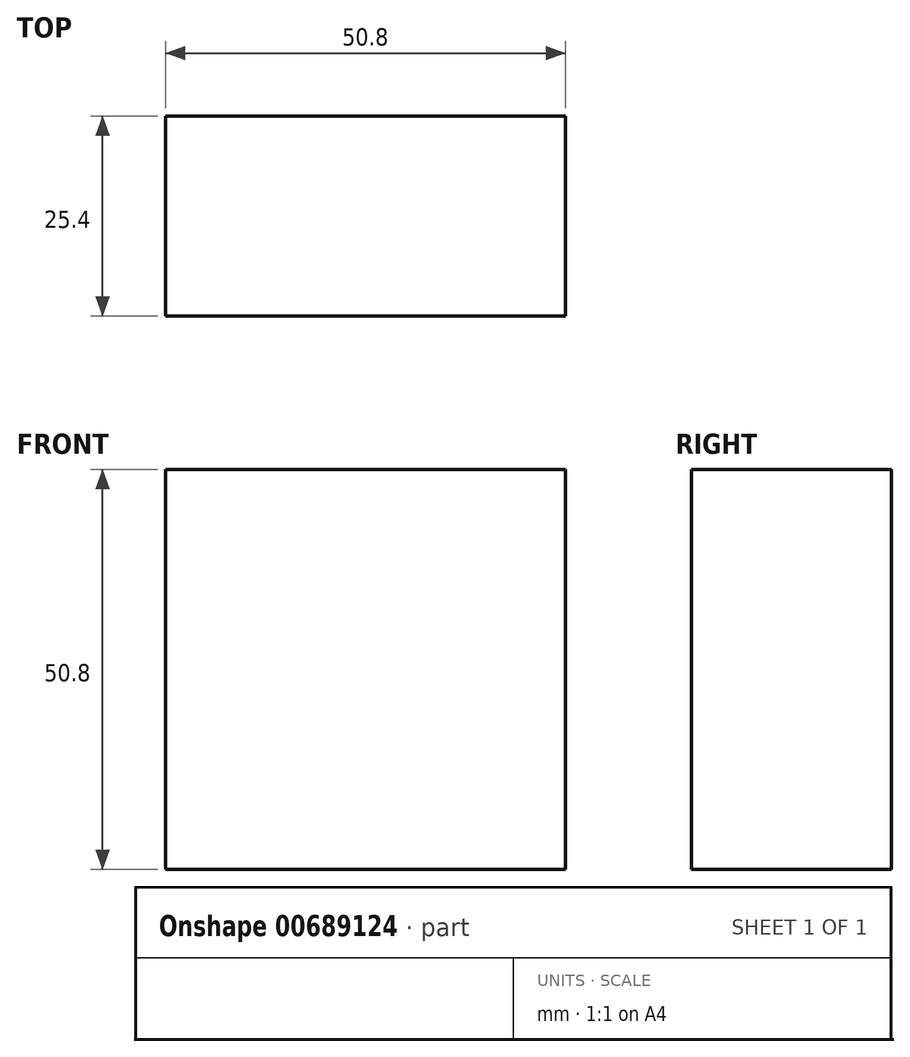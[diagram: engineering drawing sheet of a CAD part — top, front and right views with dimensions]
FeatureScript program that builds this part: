
annotation { "Feature Type Name" : "Feature", "Feature Type Description" : "" }
export const myFeature = defineFeature(function(context is Context, id is Id, definition is map)
    precondition{}
    {
        {
            var Q0;
            Q0=qCreatedBy(makeId("Front.planeOp"),FACE);
            var sketch = newSketch(context, id + "F0", { "sketchPlane" : qUnion([Q0])});
            skLineSegment(sketch, "E0.bottom", {"start": v(45.23, -14.55) * mm, "end": v(-5.57, -14.55) * mm});
            skLineSegment(sketch, "E0.top", {"start": v(45.23, 36.25) * mm, "end": v(-5.57, 36.25) * mm});
            skLineSegment(sketch, "E0.left", {"start": v(45.23, -14.55) * mm, "end": v(45.23, 36.25) * mm});
            skLineSegment(sketch, "E0.right", {"start": v(-5.57, -14.55) * mm, "end": v(-5.57, 36.25) * mm});
            skSolve(sketch);
        }
        {
            var Q0;
            Q0 = qSketchRegion(id + "F0", true);
            extrude(context, id + "F1", {"entities" : qUnion([Q0]), "depth" : 25.4 * mm, "offsetDistance" : 25.4 * mm});
        }
        {
            var Q0;
            Q0=qCreatedBy(makeId("Front.planeOp"),FACE);
            var sketch = newSketch(context, id + "F2", { "sketchPlane" : qUnion([Q0])});
            skCircle(sketch, "E1", {"center": v(17.85, 11.34) * mm, "radius": 12.7 * mm});
            skSolve(sketch);
        }
        {
            var Q0;
            Q0 = qSketchRegion(id + "F2", true);
            extrude(context, id + "F3", {"entities" : qUnion([Q0]), "operationType" : NewBodyOperationType.REMOVE, "oppositeDirection" : true, "depth" : 50.8 * mm, "offsetDistance" : 25.4 * mm});
        }
        {
            var Q0;
            Q0=qCreatedBy(makeId("Front.planeOp"),FACE);
            var sketch = newSketch(context, id + "F4", { "sketchPlane" : qUnion([Q0])});
            skCircle(sketch, "E2", {"center": v(18.04, 12.85) * mm, "radius": 12.7 * mm});
            skSolve(sketch);
        }
        {
            var Q0;
            Q0 = qSketchRegion(id + "F4", true);
            extrude(context, id + "F5", {"entities" : qUnion([Q0]), "operationType" : NewBodyOperationType.REMOVE, "oppositeDirection" : true, "depth" : 50.8 * mm, "offsetDistance" : 25.4 * mm});
        }
    });
